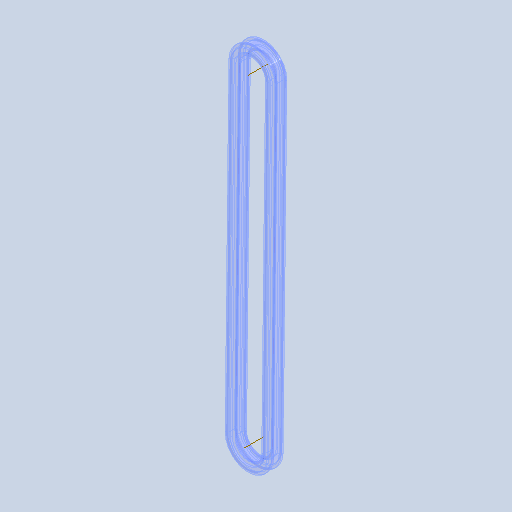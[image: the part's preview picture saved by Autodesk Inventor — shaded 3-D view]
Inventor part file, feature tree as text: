
AUTODESK INVENTOR PART (.ipt)
format: ipt  version: 2022.1 (Build 261234000, 234)  size: 156,672 bytes
history: native  units: mm
features: other x4, plane x2, sweep x1, pattern_linear x1, sketch x1
ambient origin geometry x8: Origin, YZ Plane, XZ Plane, XY Plane, X Axis, Y Axis, Z Axis, Center Point
bodies: Solid1 (feature_tree)
feature tree (9):
  other  "Eje de trabajo1"
  other  "Eje de trabajo2"
  plane  "Plano de trabajo2"
  plane  "Plano de trabajo3"
  other  "Trayectoria"
  other  "Plano de sección"
  sweep  "Sólido"
  pattern_linear  "Strand Pattern"  Spacing1=10.0mm  [1 undecoded]
  sketch  "Boceto de sección"  dims[d2=0.0mm d4=0.0mm d21=10.0mm d22=15.0mm d23=18.0mm d24=5.0mm d28=10.0mm d30=32.0mm d31=24.0mm d32=36.0mm d33=0.0mm d34=0.0mm d35=0.0mm d36=0.0mm d37=0.0mm]
note: 1 required parameter value undecoded (feature->parameter linkage not recoverable at this tier; creation-order binding heuristic only, values carry confidence <= 0.55)
